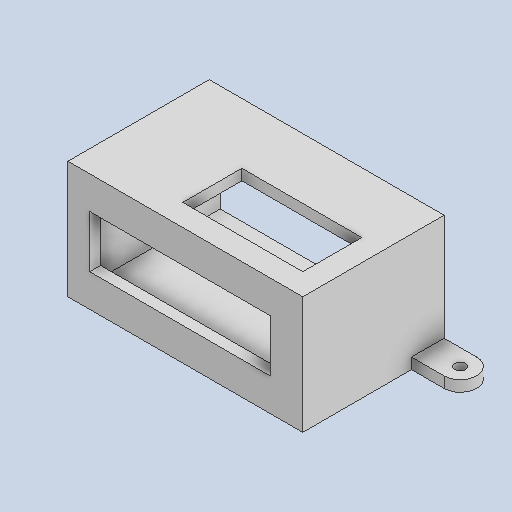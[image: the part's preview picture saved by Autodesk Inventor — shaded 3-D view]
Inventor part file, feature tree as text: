
AUTODESK INVENTOR PART (.ipt)
format: ipt  version: 2023 (Build 270158000, 158)  size: 165,888 bytes
history: native  units: mm
features: extrude x4, sketch x4
ambient origin geometry x8: Origin, YZ Plane, XZ Plane, XY Plane, X Axis, Y Axis, Z Axis, Center Point
bodies: Solid1 (feature_tree)
feature tree (8):
  extrude  "Extrusion1"  Depth=44.0mm
  extrude  "Extrusion2"  Depth=5.0mm
  extrude  "Extrusion4"  Depth=5.0mm
  extrude  "Extrusion5"  Depth=5.0mm TaperAngle=0.0deg
  sketch  "Sketch1"  dims[d0=98.0mm d1=44.0mm]
  sketch  "Sketch2"  dims[d2=5.0mm d3=5.0mm]
  sketch  "Sketch4"  dims[d4=5.0mm d5=5.0mm]
  sketch  "Sketch5"  dims[d6=60.0mm d7=0.0mm d8=5.0mm d9=0.0mm d10=10.0mm d11=15.0mm d12=15.0mm d13=15.0mm d19=27.2mm d20=55.2mm d21=10.0mm d22=10.0mm d23=10.0mm d24=0.0mm d25=15.0mm d26=5.0mm d27=15.0mm d28=5.0mm d29=0.0mm]
